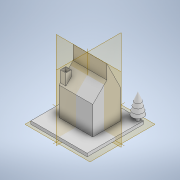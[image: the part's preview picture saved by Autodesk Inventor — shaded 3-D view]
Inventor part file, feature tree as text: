
AUTODESK INVENTOR PART (.ipt)
format: ipt  version: 2022.4 (Build 264492010, 492A)  size: 179,200 bytes
history: native  units: mm
features: sketch x6, extrude x4, plane x1, revolve x1
ambient origin geometry x8: Origin, YZ Plane, XZ Plane, XY Plane, X Axis, Y Axis, Z Axis, Center Point
bodies: Solid1 (feature_tree)
feature tree (12):
  extrude  "Extrusion1"  Depth=11.0mm
  extrude  "Extrusion2"  Depth=200.0mm TaperAngle=0.0deg
  extrude  "Extrusion3"  Depth=40.0mm
  extrude  "Extrusion4"  TaperAngle=0.0deg  [1 undecoded]
  sketch  "Sketch5"  dims[d9=50.0mm d10=50.0mm]
  plane  "Work Plane1"
  revolve  "Revolution1"  [1 undecoded]
  sketch  "Sketch1"  dims[d0=200.0mm d1=11.0mm]
  sketch  "Sketch2"  dims[d2=0.0mm d3=200.0mm d4=0.0mm]
  sketch  "Sketch3"  dims[d5=100.0mm d6=40.0mm]
  sketch  "Sketch4"  dims[d7=100.0mm d8=0.0mm]
  sketch  "Sketch7"  dims[d11=100.0mm d12=50.0mm d13=120.0mm d14=0.0mm d15=20.0mm d16=20.0mm d17=4.393mm d18=20.0mm d19=0.0mm d20=2.0mm d21=20.0mm d22=0.0mm d23=10.0mm d24=10.0mm d25=20.0mm d26=5.0mm d27=20.0mm d28=15.0mm d29=15.0mm d30=90.0deg]
note: 2 required parameter values undecoded (feature->parameter linkage not recoverable at this tier; creation-order binding heuristic only, values carry confidence <= 0.55)